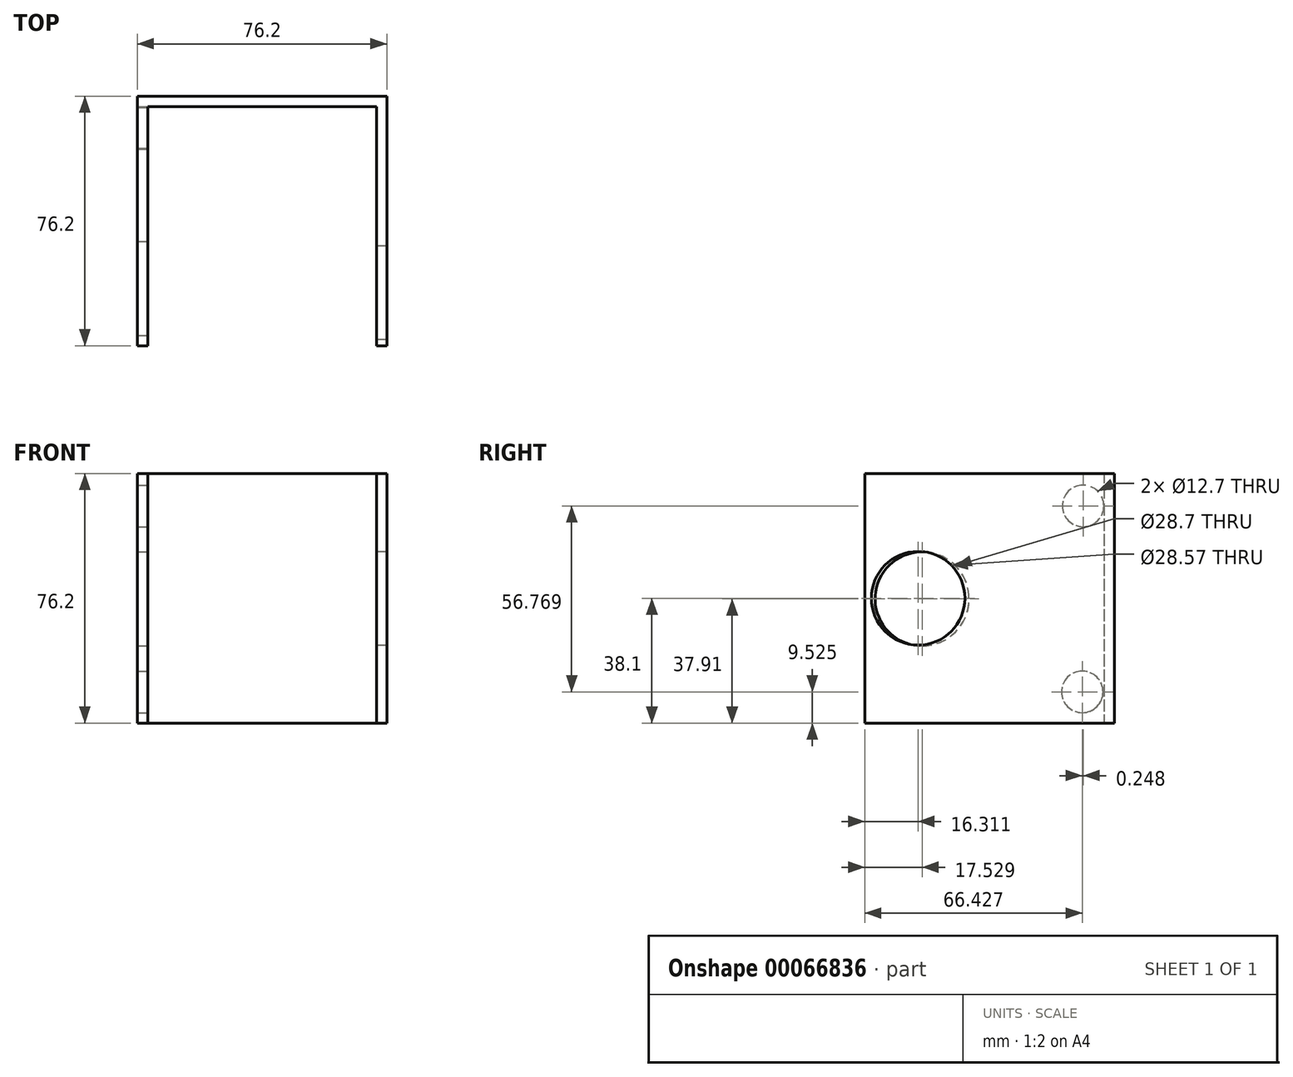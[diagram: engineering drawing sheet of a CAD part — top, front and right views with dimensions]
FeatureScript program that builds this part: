
annotation { "Feature Type Name" : "Feature", "Feature Type Description" : "" }
export const myFeature = defineFeature(function(context is Context, id is Id, definition is map)
    precondition{}
    {
        {
            var Q0;
            Q0=qCreatedBy(makeId("Top.planeOp"),FACE);
            var sketch = newSketch(context, id + "F0", { "sketchPlane" : qUnion([Q0])});
            skLineSegment(sketch, "E0.bottom", {"start": v(0, 0) * mm, "end": v(76.2, 0) * mm});
            skLineSegment(sketch, "E0.top", {"start": v(0, 76.2) * mm, "end": v(76.2, 76.2) * mm});
            skLineSegment(sketch, "E0.left", {"start": v(0, 0) * mm, "end": v(0, 76.2) * mm});
            skLineSegment(sketch, "E0.right", {"start": v(76.2, 0) * mm, "end": v(76.2, 76.2) * mm});
            skPoint(sketch, "E0.middle", {"position": v(38.1, 38.1) * mm});
            skLineSegment(sketch, "E1.bottom", {"start": v(3.17, 3.18) * mm, "end": v(73.03, 3.18) * mm});
            skLineSegment(sketch, "E1.top", {"start": v(3.17, 73.02) * mm, "end": v(73.02, 73.02) * mm});
            skLineSegment(sketch, "E1.left", {"start": v(3.18, 3.18) * mm, "end": v(3.17, 73.02) * mm});
            skLineSegment(sketch, "E1.right", {"start": v(73.03, 3.18) * mm, "end": v(73.02, 73.02) * mm});
            skSolve(sketch);
        }
        {
            var Q0;
            Q0=makeQuery(id+"F0.imprint","IMPRINT",FACE,{"disambiguationData":[TD([[makeQuery(id+"F0.imprint","IMPRINT",EDGE,{"derivedFrom":sQuery(id+"F0.wireOp",EDGE,"E0.bottom")}),1.0]])]});
            extrude(context, id + "F1", {"entities" : qUnion([Q0]), "depth" : 76.2 * mm});
        }
        {
            var Q0;
            Q0=makeQuery(id+"F1.opExtrude","SWEPT_FACE",FACE,{"disambiguationData":[OSD([sQuery(id+"F0.wireOp",EDGE,"E0.bottom")])]});
            var sketch = newSketch(context, id + "F2", { "sketchPlane" : qUnion([Q0])});
            skLineSegment(sketch, "E2", {"start": v(3.17, 14.42) * mm, "end": v(3.17, 119.3) * mm});
            skLineSegment(sketch, "E3", {"start": v(3.18, 119.3) * mm, "end": v(73.03, 119.3) * mm});
            skLineSegment(sketch, "E4", {"start": v(73.03, 119.3) * mm, "end": v(73.03, -7.7) * mm});
            skLineSegment(sketch, "E5", {"start": v(73.03, -7.7) * mm, "end": v(3.18, -7.7) * mm});
            skLineSegment(sketch, "E6", {"start": v(3.17, -7.7) * mm, "end": v(3.17, 14.42) * mm});
            skSolve(sketch);
        }
        {
            var Q0;
            {var subQ4=sQuery(id+"F2.wireOp",EDGE,"E6");var subQ8=sQuery(id+"F2.wireOp",EDGE,"E2");var subQ10=makeQuery(id+"F2.imprint","INTERSECT",VERTEX,{"derivedFrom":[subQ8,subQ4]});Q0=makeQuery(id+"F2.imprint","IMPRINT",FACE,{"disambiguationData":[TD([[makeQuery(id+"F2.imprint","IMPRINT",EDGE,{"disambiguationData":[TD([[subQ10,-1.0]])],"derivedFrom":subQ8}),-1.0]])]});}
            extrude(context, id + "F3", {"entities" : qUnion([Q0]), "operationType" : NewBodyOperationType.REMOVE, "oppositeDirection" : true, "depth" : 25.4 * mm});
        }
        {
            var Q0;
            Q0=makeQuery(id+"F3.boolean.opBoolean","MERGE",FACE,{"derivedFrom":[makeQuery(id+"F1.opExtrude","SWEPT_FACE",FACE,{"disambiguationData":[OSD([sQuery(id+"F0.wireOp",EDGE,"E1.left")])]}),makeQuery(id+"F3.opExtrude","SWEPT_FACE",FACE,{"disambiguationData":[OSD([sQuery(id+"F2.wireOp",EDGE,"E2"),sQuery(id+"F2.wireOp",EDGE,"E6")])]})]});
            var sketch = newSketch(context, id + "F4", { "sketchPlane" : qUnion([Q0])});
            skCircle(sketch, "E7", {"center": v(66.67, 66.3) * mm, "radius": 6.35 * mm});
            skCircle(sketch, "E8", {"center": v(66.43, 9.53) * mm, "radius": 6.35 * mm});
            skLineSegment(sketch, "E9", {"start": v(66.43, 9.52) * mm, "end": v(66.67, 66.3) * mm, "construction": true});
            skCircle(sketch, "E10", {"center": v(17.53, 37.9) * mm, "radius": 14.35 * mm});
            skPoint(sketch, "E10.centerSnap0", {"position": v(66.55, 37.9) * mm});
            skSolve(sketch);
        }
        {
            var Q0;
            Q0=makeQuery(id+"F4.imprint","IMPRINT",FACE,{"disambiguationData":[TD([[makeQuery(id+"F4.imprint","IMPRINT",EDGE,{"derivedFrom":sQuery(id+"F4.wireOp",EDGE,"E7")}),1.0]])]});
            var Q1;
            Q1=makeQuery(id+"F4.imprint","IMPRINT",FACE,{"disambiguationData":[TD([[makeQuery(id+"F4.imprint","IMPRINT",EDGE,{"derivedFrom":sQuery(id+"F4.wireOp",EDGE,"E8")}),1.0]])]});
            extrude(context, id + "F5", {"entities" : qUnion([Q0, Q1]), "operationType" : NewBodyOperationType.REMOVE, "oppositeDirection" : true, "depth" : 25.4 * mm});
        }
        {
            var Q0;
            Q0=makeQuery(id+"F1.opExtrude","SWEPT_FACE",FACE,{"disambiguationData":[OSD([sQuery(id+"F0.wireOp",EDGE,"E0.right")])]});
            var sketch = newSketch(context, id + "F6", { "sketchPlane" : qUnion([Q0])});
            skCircle(sketch, "E11", {"center": v(16.31, 38.1) * mm, "radius": 14.29 * mm});
            skSolve(sketch);
        }
        {
            var Q0;
            Q0=makeQuery(id+"F4.imprint","IMPRINT",FACE,{"disambiguationData":[TD([[makeQuery(id+"F4.imprint","IMPRINT",EDGE,{"derivedFrom":sQuery(id+"F4.wireOp",EDGE,"E10")}),1.0]])]});
            extrude(context, id + "F7", {"entities" : qUnion([Q0]), "operationType" : NewBodyOperationType.REMOVE, "oppositeDirection" : true, "depth" : 25.4 * mm});
        }
        {
            var Q0;
            Q0=makeQuery(id+"F6.imprint","IMPRINT",FACE,{"disambiguationData":[TD([[makeQuery(id+"F6.imprint","IMPRINT",EDGE,{"derivedFrom":sQuery(id+"F6.wireOp",EDGE,"E11")}),1.0]])]});
            extrude(context, id + "F8", {"entities" : qUnion([Q0]), "operationType" : NewBodyOperationType.REMOVE, "oppositeDirection" : true, "depth" : 25.4 * mm});
        }
    });
